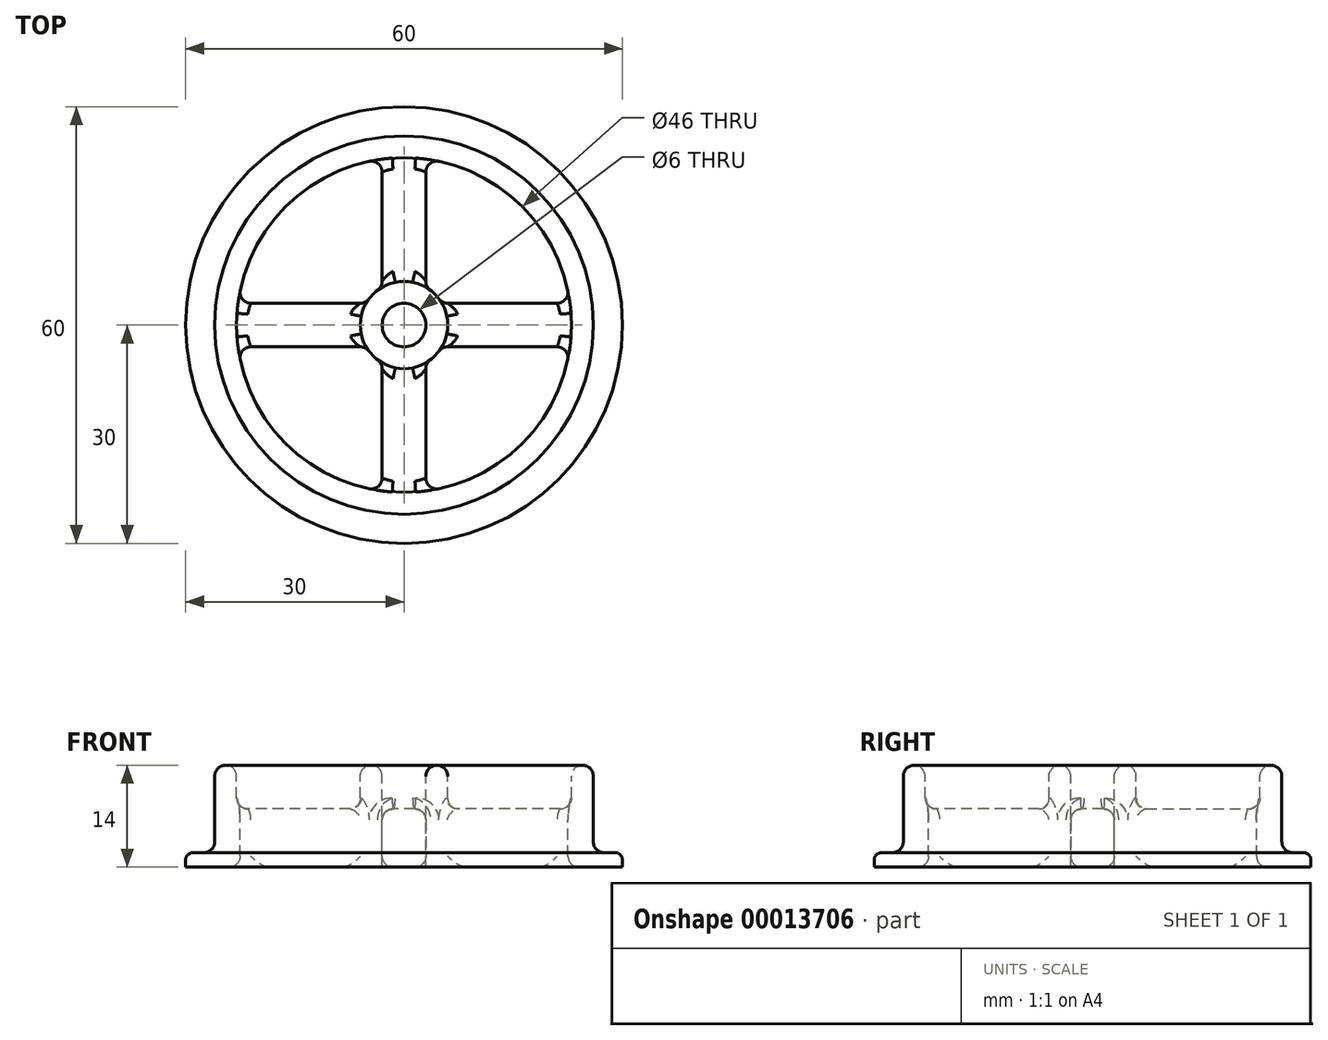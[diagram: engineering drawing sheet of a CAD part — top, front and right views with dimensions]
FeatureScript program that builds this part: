
annotation { "Feature Type Name" : "Feature", "Feature Type Description" : "" }
export const myFeature = defineFeature(function(context is Context, id is Id, definition is map)
    precondition{}
    {
        {
            var Q0;
            Q0=qCreatedBy(makeId("Top.planeOp"),FACE);
            var sketch = newSketch(context, id + "F0", { "sketchPlane" : qUnion([Q0])});
            skCircle(sketch, "E0", {"center": v(0, 0) * mm, "radius": 30 * mm});
            skCircle(sketch, "E1", {"center": v(0, 0) * mm, "radius": 26 * mm});
            skCircle(sketch, "E2", {"center": v(0, 0) * mm, "radius": 6 * mm});
            skCircle(sketch, "E3", {"center": v(0, 0) * mm, "radius": 3 * mm});
            skCircle(sketch, "E4", {"center": v(0, 0) * mm, "radius": 23 * mm});
            skLineSegment(sketch, "E5", {"start": v(-5.2, 3) * mm, "end": v(-22.8, 3) * mm});
            skLineSegment(sketch, "E6", {"start": v(-5.2, -3) * mm, "end": v(-22.8, -3) * mm});
            skLineSegment(sketch, "E7", {"start": v(-3, 5.2) * mm, "end": v(-3, 22.8) * mm});
            skLineSegment(sketch, "E8", {"start": v(3, 5.2) * mm, "end": v(3, 22.8) * mm});
            skLineSegment(sketch, "E9", {"start": v(5.2, 3) * mm, "end": v(22.8, 3) * mm});
            skLineSegment(sketch, "E10", {"start": v(22.8, -3) * mm, "end": v(5.2, -3) * mm});
            skLineSegment(sketch, "E11", {"start": v(-3, -5.2) * mm, "end": v(-3, -22.8) * mm});
            skLineSegment(sketch, "E12", {"start": v(3, -5.2) * mm, "end": v(3, -22.8) * mm});
            skSolve(sketch);
        }
        {
            var Q0;
            {var subQ1=sQuery(id+"F0.wireOp",EDGE,"E7");Q0=makeQuery(id+"F0.imprint","IMPRINT",FACE,{"disambiguationData":[TD([[makeQuery(id+"F0.imprint","IMPRINT",EDGE,{"derivedFrom":subQ1}),-1.0]])]});}
            var Q1;
            {var subQ1=sQuery(id+"F0.wireOp",EDGE,"E5");Q1=makeQuery(id+"F0.imprint","IMPRINT",FACE,{"disambiguationData":[TD([[makeQuery(id+"F0.imprint","IMPRINT",EDGE,{"derivedFrom":subQ1}),1.0]])]});}
            var Q2;
            {var subQ1=sQuery(id+"F0.wireOp",EDGE,"E11");Q2=makeQuery(id+"F0.imprint","IMPRINT",FACE,{"disambiguationData":[TD([[makeQuery(id+"F0.imprint","IMPRINT",EDGE,{"derivedFrom":subQ1}),1.0]])]});}
            var Q3;
            {var subQ1=sQuery(id+"F0.wireOp",EDGE,"E9");Q3=makeQuery(id+"F0.imprint","IMPRINT",FACE,{"disambiguationData":[TD([[makeQuery(id+"F0.imprint","IMPRINT",EDGE,{"derivedFrom":subQ1}),-1.0]])]});}
            var Q4;
            Q4=makeQuery(id+"F0.imprint","IMPRINT",FACE,{"disambiguationData":[TD([[makeQuery(id+"F0.imprint","IMPRINT",EDGE,{"derivedFrom":sQuery(id+"F0.wireOp",EDGE,"E0")}),1.0]])]});
            var Q5;
            Q5=makeQuery(id+"F0.imprint","IMPRINT",FACE,{"disambiguationData":[TD([[makeQuery(id+"F0.imprint","IMPRINT",EDGE,{"derivedFrom":sQuery(id+"F0.wireOp",EDGE,"E1")}),1.0]])]});
            var Q6;
            Q6=makeQuery(id+"F0.imprint","IMPRINT",FACE,{"disambiguationData":[TD([[makeQuery(id+"F0.imprint","IMPRINT",EDGE,{"derivedFrom":sQuery(id+"F0.wireOp",EDGE,"E3")}),-1.0]])]});
            extrude(context, id + "F1", {"entities" : qUnion([Q0, Q1, Q2, Q3, Q4, Q5, Q6]), "oppositeDirection" : true, "depth" : 2 * mm});
        }
        {
            var Q0;
            Q0=makeQuery(id+"F0.imprint","IMPRINT",FACE,{"disambiguationData":[TD([[makeQuery(id+"F0.imprint","IMPRINT",EDGE,{"derivedFrom":sQuery(id+"F0.wireOp",EDGE,"E1")}),1.0]])]});
            var Q1;
            Q1=makeQuery(id+"F0.imprint","IMPRINT",FACE,{"disambiguationData":[TD([[makeQuery(id+"F0.imprint","IMPRINT",EDGE,{"derivedFrom":sQuery(id+"F0.wireOp",EDGE,"E3")}),-1.0]])]});
            extrude(context, id + "F2", {"entities" : qUnion([Q0, Q1]), "operationType" : NewBodyOperationType.ADD, "depth" : 12 * mm});
        }
        {
            var Q0;
            {var subQ1=sQuery(id+"F0.wireOp",EDGE,"E5");Q0=makeQuery(id+"F0.imprint","IMPRINT",FACE,{"disambiguationData":[TD([[makeQuery(id+"F0.imprint","IMPRINT",EDGE,{"derivedFrom":subQ1}),1.0]])]});}
            var Q1;
            {var subQ1=sQuery(id+"F0.wireOp",EDGE,"E7");Q1=makeQuery(id+"F0.imprint","IMPRINT",FACE,{"disambiguationData":[TD([[makeQuery(id+"F0.imprint","IMPRINT",EDGE,{"derivedFrom":subQ1}),-1.0]])]});}
            var Q2;
            {var subQ1=sQuery(id+"F0.wireOp",EDGE,"E9");Q2=makeQuery(id+"F0.imprint","IMPRINT",FACE,{"disambiguationData":[TD([[makeQuery(id+"F0.imprint","IMPRINT",EDGE,{"derivedFrom":subQ1}),-1.0]])]});}
            var Q3;
            {var subQ1=sQuery(id+"F0.wireOp",EDGE,"E11");Q3=makeQuery(id+"F0.imprint","IMPRINT",FACE,{"disambiguationData":[TD([[makeQuery(id+"F0.imprint","IMPRINT",EDGE,{"derivedFrom":subQ1}),1.0]])]});}
            extrude(context, id + "F3", {"entities" : qUnion([Q0, Q1, Q2, Q3]), "operationType" : NewBodyOperationType.ADD, "depth" : 6 * mm});
        }
        {
            var Q0;
            {var subQ0=sQuery(id+"F0.wireOp",EDGE,"E2");Q0=makeQuery(id+"F2.boolean.opBoolean","MERGE",FACE,{"derivedFrom":[makeQuery(id+"F1.opExtrude","SWEPT_FACE",FACE,{"disambiguationData":[OSD([subQ0]),TDD([makeQuery(id+"F0.imprint","IMPRINT",EDGE,{"disambiguationData":[TD([[makeQuery(id+"F0.imprint","INTERSECT",VERTEX,{"derivedFrom":[subQ0,sQuery(id+"F0.wireOp",EDGE,"E8")]}),1.0]])],"derivedFrom":subQ0})])]}),makeQuery(id+"F1.opExtrude","SWEPT_FACE",FACE,{"disambiguationData":[OSD([subQ0]),TDD([makeQuery(id+"F0.imprint","IMPRINT",EDGE,{"disambiguationData":[TD([[makeQuery(id+"F0.imprint","INTERSECT",VERTEX,{"derivedFrom":[subQ0,sQuery(id+"F0.wireOp",EDGE,"E5")]}),1.0]])],"derivedFrom":subQ0})])]}),makeQuery(id+"F1.opExtrude","SWEPT_FACE",FACE,{"disambiguationData":[OSD([subQ0]),TDD([makeQuery(id+"F0.imprint","IMPRINT",EDGE,{"disambiguationData":[TD([[makeQuery(id+"F0.imprint","INTERSECT",VERTEX,{"derivedFrom":[subQ0,sQuery(id+"F0.wireOp",EDGE,"E6")]}),-1.0]])],"derivedFrom":subQ0})])]}),makeQuery(id+"F1.opExtrude","SWEPT_FACE",FACE,{"disambiguationData":[OSD([subQ0]),TDD([makeQuery(id+"F0.imprint","IMPRINT",EDGE,{"disambiguationData":[TD([[makeQuery(id+"F0.imprint","INTERSECT",VERTEX,{"derivedFrom":[subQ0,sQuery(id+"F0.wireOp",EDGE,"E10")]}),1.0]])],"derivedFrom":subQ0})])]}),makeQuery(id+"F2.opExtrude","SWEPT_FACE",FACE,{"disambiguationData":[OSD([subQ0])]})]});}
            var Q1;
            {var subQ0=sQuery(id+"F0.wireOp",EDGE,"E4");Q1=makeQuery(id+"F2.boolean.opBoolean","MERGE",FACE,{"derivedFrom":[makeQuery(id+"F1.opExtrude","SWEPT_FACE",FACE,{"disambiguationData":[OSD([subQ0]),TDD([makeQuery(id+"F0.imprint","IMPRINT",EDGE,{"disambiguationData":[TD([[makeQuery(id+"F0.imprint","INTERSECT",VERTEX,{"derivedFrom":[subQ0,sQuery(id+"F0.wireOp",EDGE,"E8")]}),1.0]])],"derivedFrom":subQ0})])]}),makeQuery(id+"F1.opExtrude","SWEPT_FACE",FACE,{"disambiguationData":[OSD([subQ0]),TDD([makeQuery(id+"F0.imprint","IMPRINT",EDGE,{"disambiguationData":[TD([[makeQuery(id+"F0.imprint","INTERSECT",VERTEX,{"derivedFrom":[subQ0,sQuery(id+"F0.wireOp",EDGE,"E5")]}),1.0]])],"derivedFrom":subQ0})])]}),makeQuery(id+"F1.opExtrude","SWEPT_FACE",FACE,{"disambiguationData":[OSD([subQ0]),TDD([makeQuery(id+"F0.imprint","IMPRINT",EDGE,{"disambiguationData":[TD([[makeQuery(id+"F0.imprint","INTERSECT",VERTEX,{"derivedFrom":[subQ0,sQuery(id+"F0.wireOp",EDGE,"E6")]}),-1.0]])],"derivedFrom":subQ0})])]}),makeQuery(id+"F1.opExtrude","SWEPT_FACE",FACE,{"disambiguationData":[OSD([subQ0]),TDD([makeQuery(id+"F0.imprint","IMPRINT",EDGE,{"disambiguationData":[TD([[makeQuery(id+"F0.imprint","INTERSECT",VERTEX,{"derivedFrom":[subQ0,sQuery(id+"F0.wireOp",EDGE,"E10")]}),1.0]])],"derivedFrom":subQ0})])]}),makeQuery(id+"F2.opExtrude","SWEPT_FACE",FACE,{"disambiguationData":[OSD([subQ0])]})]});}
            var Q2;
            Q2=makeQuery(id+"F3.opExtrude","CAP_FACE",FACE,{"disambiguationData":[OSD([sQuery(id+"F0.wireOp",EDGE,"E2"),sQuery(id+"F0.wireOp",EDGE,"E4"),sQuery(id+"F0.wireOp",EDGE,"E5"),sQuery(id+"F0.wireOp",EDGE,"E6")])],"isStart":false});
            var Q3;
            Q3=makeQuery(id+"F3.opExtrude","CAP_FACE",FACE,{"disambiguationData":[OSD([sQuery(id+"F0.wireOp",EDGE,"E2"),sQuery(id+"F0.wireOp",EDGE,"E4"),sQuery(id+"F0.wireOp",EDGE,"E9"),sQuery(id+"F0.wireOp",EDGE,"E10")])],"isStart":false});
            var Q4;
            Q4=makeQuery(id+"F3.opExtrude","CAP_FACE",FACE,{"disambiguationData":[OSD([sQuery(id+"F0.wireOp",EDGE,"E2"),sQuery(id+"F0.wireOp",EDGE,"E4"),sQuery(id+"F0.wireOp",EDGE,"E11"),sQuery(id+"F0.wireOp",EDGE,"E12")])],"isStart":false});
            var Q5;
            Q5=makeQuery(id+"F3.opExtrude","CAP_FACE",FACE,{"disambiguationData":[OSD([sQuery(id+"F0.wireOp",EDGE,"E2"),sQuery(id+"F0.wireOp",EDGE,"E4"),sQuery(id+"F0.wireOp",EDGE,"E7"),sQuery(id+"F0.wireOp",EDGE,"E8")])],"isStart":false});
            var Q6;
            Q6=makeQuery(id+"F2.opExtrude","SWEPT_FACE",FACE,{"disambiguationData":[OSD([sQuery(id+"F0.wireOp",EDGE,"E1")])]});
            var Q7;
            Q7=makeQuery(id+"F2.opExtrude","CAP_EDGE",EDGE,{"disambiguationData":[OSD([sQuery(id+"F0.wireOp",EDGE,"E3")])],"isStart":false});
            fillet(context, id + "F4", {"entities" : qUnion([Q0, Q1, Q2, Q3, Q4, Q5, Q6, Q7]), "radius" : 1.5 * mm, "tangentPropagation" : true, "allowEdgeOverflow" : false});
        }
        {
            var Q0;
            Q0=makeQuery(id+"F1.opExtrude","CAP_EDGE",EDGE,{"disambiguationData":[OSD([sQuery(id+"F0.wireOp",EDGE,"E0")])],"isStart":true});
            fillet(context, id + "F5", {"entities" : qUnion([Q0]), "radius" : 1 * mm, "tangentPropagation" : true, "allowEdgeOverflow" : false});
        }
    });
